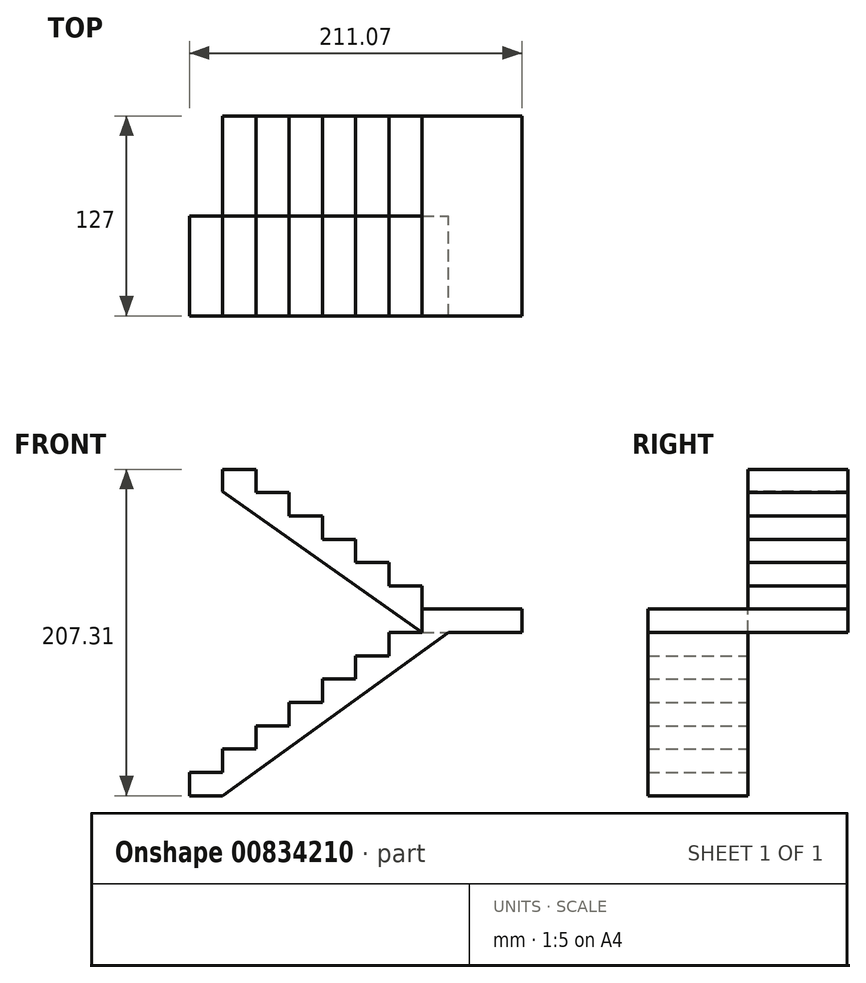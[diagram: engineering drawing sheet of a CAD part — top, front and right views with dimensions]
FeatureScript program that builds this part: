
annotation { "Feature Type Name" : "Feature", "Feature Type Description" : "" }
export const myFeature = defineFeature(function(context is Context, id is Id, definition is map)
    precondition{}
    {
        {
            var Q0;
            Q0=qCreatedBy(makeId("Front.planeOp"),FACE);
            var sketch = newSketch(context, id + "F0", { "sketchPlane" : qUnion([Q0])});
            skLineSegment(sketch, "E0", {"start": v(-177.55, -100.16) * mm, "end": v(-177.55, -85.35) * mm});
            skLineSegment(sketch, "E1", {"start": v(-177.55, -85.35) * mm, "end": v(-156.47, -85.35) * mm});
            skLineSegment(sketch, "E2", {"start": v(-156.47, -85.35) * mm, "end": v(-156.47, -70.55) * mm});
            skLineSegment(sketch, "E3", {"start": v(-156.47, -70.55) * mm, "end": v(-135.39, -70.55) * mm});
            skLineSegment(sketch, "E4", {"start": v(-135.39, -70.55) * mm, "end": v(-135.39, -55.74) * mm});
            skLineSegment(sketch, "E5", {"start": v(-135.39, -55.74) * mm, "end": v(-114.3, -55.74) * mm});
            skLineSegment(sketch, "E6", {"start": v(-114.3, -55.74) * mm, "end": v(-114.3, -40.93) * mm});
            skLineSegment(sketch, "E7", {"start": v(-114.3, -40.93) * mm, "end": v(-93.22, -40.93) * mm});
            skLineSegment(sketch, "E8", {"start": v(-93.22, -40.93) * mm, "end": v(-93.22, -26.12) * mm});
            skLineSegment(sketch, "E9", {"start": v(-93.22, -26.12) * mm, "end": v(-72.14, -26.12) * mm});
            skLineSegment(sketch, "E10", {"start": v(-72.14, -26.12) * mm, "end": v(-72.14, -11.31) * mm});
            skLineSegment(sketch, "E11", {"start": v(-72.14, -11.31) * mm, "end": v(-51.06, -11.31) * mm});
            skLineSegment(sketch, "E12", {"start": v(-51.06, -11.31) * mm, "end": v(-51.06, 3.5) * mm});
            skLineSegment(sketch, "E13", {"start": v(-51.06, 3.5) * mm, "end": v(-29.98, 3.5) * mm});
            skLineSegment(sketch, "E14", {"start": v(-29.98, 3.5) * mm, "end": v(-29.98, 18.3) * mm});
            skLineSegment(sketch, "E15", {"start": v(-29.98, 18.3) * mm, "end": v(33.52, 18.3) * mm});
            skLineSegment(sketch, "E16", {"start": v(-29.98, 18.3) * mm, "end": v(-29.98, 33.11) * mm});
            skLineSegment(sketch, "E17", {"start": v(-29.98, 33.11) * mm, "end": v(-51.06, 33.11) * mm});
            skLineSegment(sketch, "E18", {"start": v(-51.06, 33.11) * mm, "end": v(-51.06, 47.92) * mm});
            skLineSegment(sketch, "E19", {"start": v(-51.06, 47.92) * mm, "end": v(-72.14, 47.92) * mm});
            skLineSegment(sketch, "E20", {"start": v(-72.14, 47.92) * mm, "end": v(-72.14, 62.73) * mm});
            skLineSegment(sketch, "E21", {"start": v(-72.14, 62.73) * mm, "end": v(-93.22, 62.73) * mm});
            skLineSegment(sketch, "E22", {"start": v(-93.22, 62.73) * mm, "end": v(-93.22, 77.54) * mm});
            skLineSegment(sketch, "E23", {"start": v(-93.22, 77.54) * mm, "end": v(-114.3, 77.54) * mm});
            skLineSegment(sketch, "E24", {"start": v(-114.3, 77.54) * mm, "end": v(-114.3, 92.34) * mm});
            skLineSegment(sketch, "E25", {"start": v(-114.3, 92.34) * mm, "end": v(-135.39, 92.34) * mm});
            skLineSegment(sketch, "E26", {"start": v(-135.39, 92.34) * mm, "end": v(-135.39, 107.15) * mm});
            skLineSegment(sketch, "E27", {"start": v(-135.39, 107.15) * mm, "end": v(-156.47, 107.15) * mm});
            skLineSegment(sketch, "E28", {"start": v(33.52, 18.3) * mm, "end": v(33.52, 3.5) * mm});
            skLineSegment(sketch, "E29", {"start": v(33.52, 3.5) * mm, "end": v(-13.26, 3.5) * mm});
            skLineSegment(sketch, "E30", {"start": v(-177.55, -100.16) * mm, "end": v(-156.47, -100.16) * mm});
            skLineSegment(sketch, "E31", {"start": v(-156.47, -100.16) * mm, "end": v(-13.26, 3.5) * mm});
            skLineSegment(sketch, "E32", {"start": v(-29.98, 3.5) * mm, "end": v(-156.47, 93.08) * mm});
            skLineSegment(sketch, "E33", {"start": v(-29.98, 3.5) * mm, "end": v(-13.26, 3.5) * mm});
            skLineSegment(sketch, "E34", {"start": v(-156.47, 107.15) * mm, "end": v(-156.47, 93.08) * mm});
            skPoint(sketch, "E35.start.orphan", {"position": v(-156.47, 121.96) * mm});
            skSolve(sketch);
        }
        {
            var Q0;
            Q0=makeQuery(id+"F0.imprint","IMPRINT",FACE,{"disambiguationData":[TD([[makeQuery(id+"F0.imprint","IMPRINT",EDGE,{"derivedFrom":sQuery(id+"F0.wireOp",EDGE,"E0")}),-1.0]])]});
            var Q1;
            Q1=makeQuery(id+"F0.imprint","IMPRINT",FACE,{"disambiguationData":[TD([[makeQuery(id+"F0.imprint","IMPRINT",EDGE,{"derivedFrom":sQuery(id+"F0.wireOp",EDGE,"E14")}),-1.0]])]});
            extrude(context, id + "F1", {"entities" : qUnion([Q0, Q1]), "depth" : 63.5 * mm, "offsetDistance" : 25.4 * mm});
        }
        {
            var Q0;
            Q0=makeQuery(id+"F0.imprint","IMPRINT",FACE,{"disambiguationData":[TD([[makeQuery(id+"F0.imprint","IMPRINT",EDGE,{"derivedFrom":sQuery(id+"F0.wireOp",EDGE,"E14")}),1.0]])]});
            var Q1;
            Q1=makeQuery(id+"F0.imprint","IMPRINT",FACE,{"disambiguationData":[TD([[makeQuery(id+"F0.imprint","IMPRINT",EDGE,{"derivedFrom":sQuery(id+"F0.wireOp",EDGE,"E14")}),-1.0]])]});
            extrude(context, id + "F2", {"entities" : qUnion([Q0, Q1]), "operationType" : NewBodyOperationType.ADD, "oppositeDirection" : true, "depth" : 63.5 * mm, "offsetDistance" : 25.4 * mm});
        }
    });
